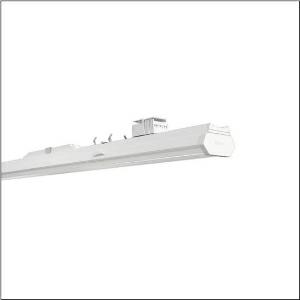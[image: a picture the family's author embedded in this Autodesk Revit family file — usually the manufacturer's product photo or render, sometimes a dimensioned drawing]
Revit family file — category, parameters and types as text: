
# Revit family: licross_r__11_protected_mo_51tp12cn58xf_fcc9
name_source: partatom
category: Lighting Fixtures
units: mm (PartAtom-declared; Revit-internal decimal feet)

## family parameters
Cut with Voids When Loaded = No
Host = Face
Light Source = No
Part Type = Normal
Room Calculation Point = No
Round Connector Dimension = Use Diameter
Shared = No

## types (1)
- --- (1 x LED, 8190 lm, 49 W, 5000K)
    Apparent Load = 49 VA
    CIE Flux Codes = 73 92 98 99 100
    Color Rendering = 80
    Color Temperature = 5000K
    Default Elevation = 1800 mm
    Description = Licross® 11 Protected MO, luminaire insert, of sheet steel, galvanised, coil coated, white, length: 1.500mm, width: 90mm, height: 101mm, LED rated luminous flux: 8.190lm, light colour: 850, control gear: ON/OFF Multilumen, CLOi, control gear: ECG Multilumen, with plug, 3-pole, with phase selection, mains connection: 220..240V, AC, 50/60Hz, start of lifetime: 49W, end of service life: 54W, halogen-free wiring, primary optical cover: cover, of PMMA, light emission: direct distribution, primary light characteristic: symmetric, protection rating (complete): IP64, insulation class (complete): insulation class I (protective earthing), certification: CE, ENEC, VDE, UKCA, protection symbol: D if used in an environment with conductive dust loads with corresponding accessories, impact resistance: IK06, permissible ambient temperature for indoor applications: -35..+40°C, reducing of maximum allowable ambient temperature of 5°C with ceiling mounting, corresponds to IFS (International Featured Standards) requirements for safety and quality in the food industry, LABS conformity tested according to VDMA 24364:2018-05, packaging unit: 1 piece
    Height = 92 mm
    Lamp = 1 x LED
    Lamp Light Flux = 8190 lm
    Lamp Power = 49 W
    Lamp count = 1
    Length = 1500 mm
    Luminous efficacy = 167 lm/W
    Manufacturer = Siteco
    ModVariant = No
    Model = 51TP12CN58XF
    Mounting Place = Ceiling
    Mounting Type = Pendant
    Number of Poles = 1
    OnlyDefault = Yes
    Power Factor = 1
    Product Name = Licross® 11 Protected MO
    Product group = luminaire insert
    ProductGroupID = 902
    Protection Class = Protection class I
    Protection Degree = IP 64
    RLX_Detail_Level = 1
    RLX_Emergency_Light_Flux = 0 lm
    RLX_Emergency_Type = 0
    RLX_Emergency_Type_DB = No
    RlxData = <blob elided: 21985 chars, md5=dee8451b>
    Socket = socket
    Standby Power = 0 W
    System Light Flux = 8190 lm
    System Power = 49 W
    Type Comments = factory setting: luminous flux: 100 % | (A | C | E) | 111 mA
    Type Image = l_1256148.jpg
    URL = http://relux.com
    VarID = @adj_199754
    Voltage = 0 V
    Weight = 0.00 kg
    Width = 88 mm

## geometry (parser evidence)
native form markers: Blend x4, Sweep x12
no freeform markers — native parametric forms only
